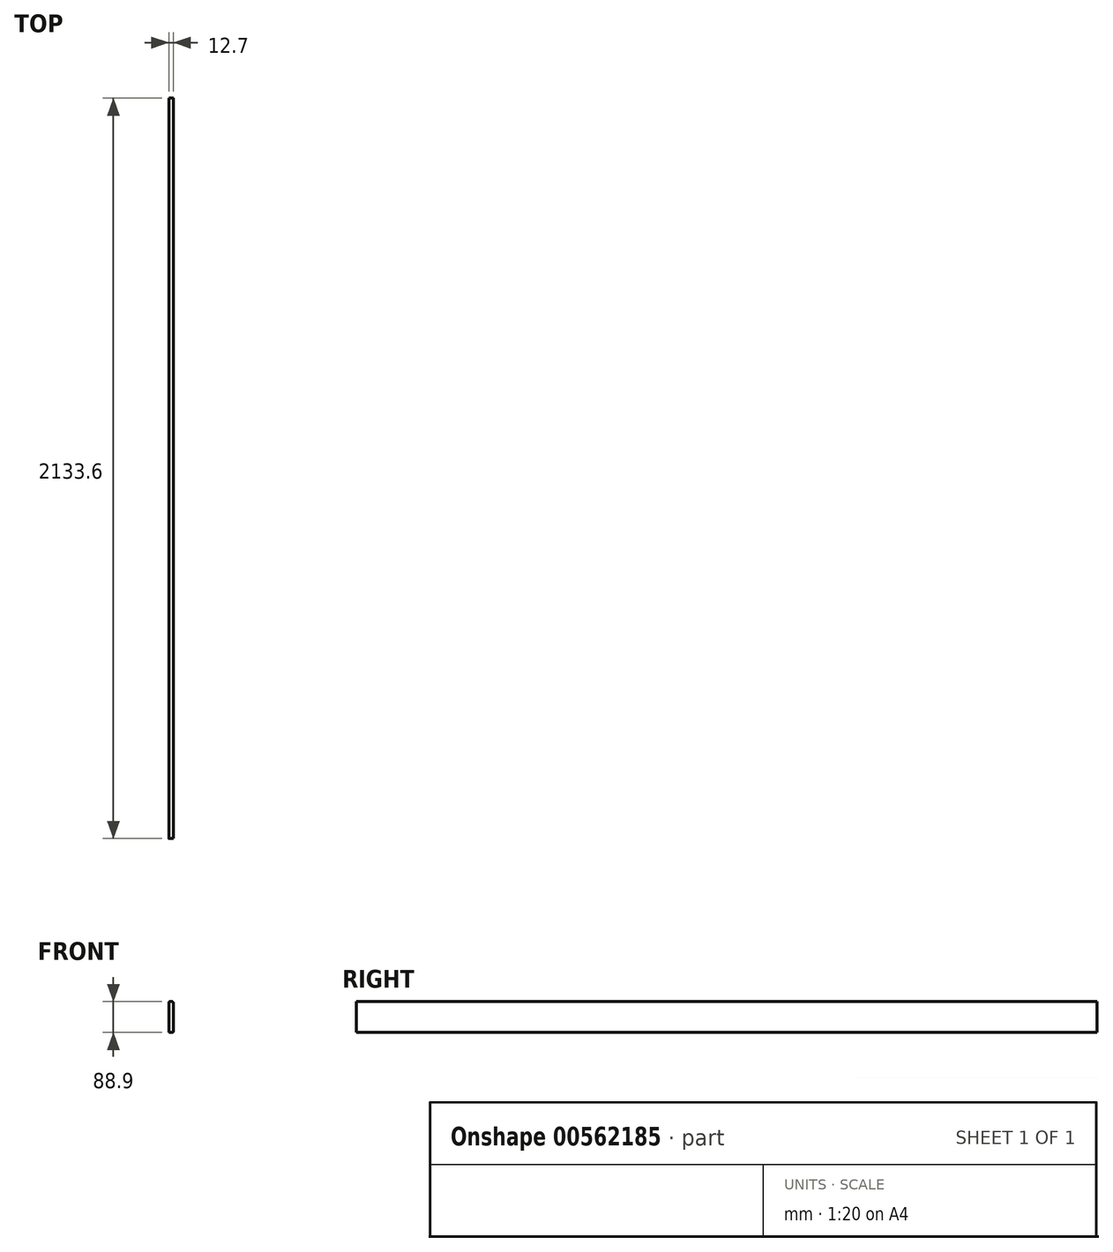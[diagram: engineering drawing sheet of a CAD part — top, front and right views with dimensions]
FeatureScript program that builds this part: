
annotation { "Feature Type Name" : "Feature", "Feature Type Description" : "" }
export const myFeature = defineFeature(function(context is Context, id is Id, definition is map)
    precondition{}
    {
        {
            var Q0;
            Q0=qCreatedBy(makeId("Front.planeOp"),FACE);
            var sketch = newSketch(context, id + "F0", { "sketchPlane" : qUnion([Q0])});
            skLineSegment(sketch, "E0.bottom", {"start": v(-3.17, 44.45) * mm, "end": v(3.17, 44.45) * mm});
            skLineSegment(sketch, "E0.top", {"start": v(-3.17, -44.45) * mm, "end": v(3.17, -44.45) * mm});
            skLineSegment(sketch, "E0.left", {"start": v(-6.35, 41.28) * mm, "end": v(-6.35, -41.28) * mm});
            skLineSegment(sketch, "E0.right", {"start": v(6.35, 41.28) * mm, "end": v(6.35, -41.28) * mm});
            skPoint(sketch, "E1.visualSharp", {"position": v(-6.35, 44.45) * mm});
            skArc(sketch, "E1.filletArc", {"start": v(-3.17, 44.45) * mm, "mid": v(-5.42, 43.52) * mm, "end": v(-6.35, 41.28) * mm});
            skPoint(sketch, "E2.visualSharp", {"position": v(6.35, 44.45) * mm});
            skArc(sketch, "E2.filletArc", {"start": v(6.35, 41.28) * mm, "mid": v(5.42, 43.52) * mm, "end": v(3.17, 44.45) * mm});
            skPoint(sketch, "E3.visualSharp", {"position": v(-6.35, -44.45) * mm});
            skArc(sketch, "E3.filletArc", {"start": v(-6.35, -41.28) * mm, "mid": v(-5.42, -43.52) * mm, "end": v(-3.17, -44.45) * mm});
            skPoint(sketch, "E4.visualSharp", {"position": v(6.35, -44.45) * mm});
            skArc(sketch, "E4.filletArc", {"start": v(3.17, -44.45) * mm, "mid": v(5.42, -43.52) * mm, "end": v(6.35, -41.28) * mm});
            skLineSegment(sketch, "E5", {"start": v(0, 0) * mm, "end": v(0, -44.45) * mm, "construction": true});
            skLineSegment(sketch, "E6", {"start": v(0, 0) * mm, "end": v(-6.35, 0) * mm, "construction": true});
            skSolve(sketch);
        }
        {
            var Q0;
            Q0=makeQuery(id+"F0.imprint","IMPRINT",FACE,{"disambiguationData":[TD([[makeQuery(id+"F0.imprint","IMPRINT",EDGE,{"derivedFrom":sQuery(id+"F0.wireOp",EDGE,"E0.bottom")}),-1.0]])]});
            extrude(context, id + "F1", {"entities" : qUnion([Q0]), "depth" : 2133.6 * mm, "offsetDistance" : 25.4 * mm});
        }
    });
